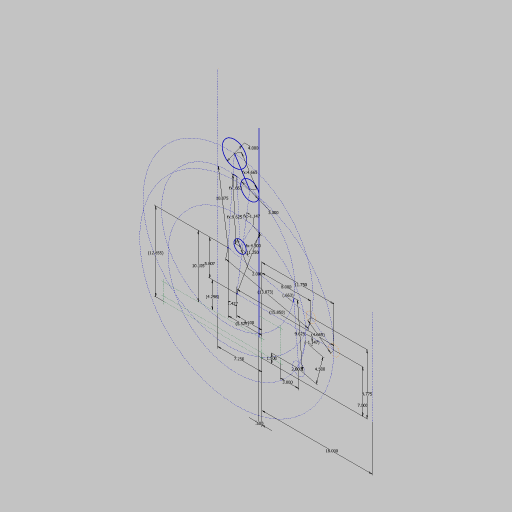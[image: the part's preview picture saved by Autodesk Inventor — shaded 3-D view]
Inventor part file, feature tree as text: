
AUTODESK INVENTOR PART (.ipt)
format: ipt  version: 2023.5 (Build 275446000, 446)  size: 171,008 bytes
history: native  units: in
note: dims shown in document units (in); Inventor stores cm internally (conversion verified against a paired STEP export)
features: sketch x3
ambient origin geometry x8: Origin, YZ Plane, XZ Plane, XY Plane, X Axis, Y Axis, Z Axis, Center Point
feature tree (3):
  sketch  "Sketch1"  dims[d0=2.0in]
  sketch  "Sketch2"  dims[d1=16.0in]
  sketch  "Sketch3"  dims[d2=0.75in d3=3.0in d4=5.0in d5=5.75in d6=2.0in d7=1.5in d8=8.0in d9=18.0in d10=11.75in d11=7.0in d12=4.5in d13=9.625in d14=9.625in d15=4.5in d16=4.6651in d18=7.25in d19=2.0in d20=6.0in d21=2.25in d22=2.0in d23=4.0in d25=11.875in d26=4.5in d27=7.5in d28=4.0in d29=0.5in d30=2.0in d31=2.0in d32=5.5in d33=6.5in d34=1.0in d35=1.0in d36=1.0in d37=1.0in d38=4.1in d39=4.2977in d40=10.105in d41=5.5273in d42=11.25in d43=10.875in d44=13.8735in d45=15.8501in d46=-1.1475in d47=1.4273in d48=5.8073in d49=12.855in d50=3.0in d51=0.5in d52=4.0in d53=2.0in d54=-1.1475in d55=3.0in d56=4.6651in d57=0.6634in d58=0.6634in d59=9.775in]
